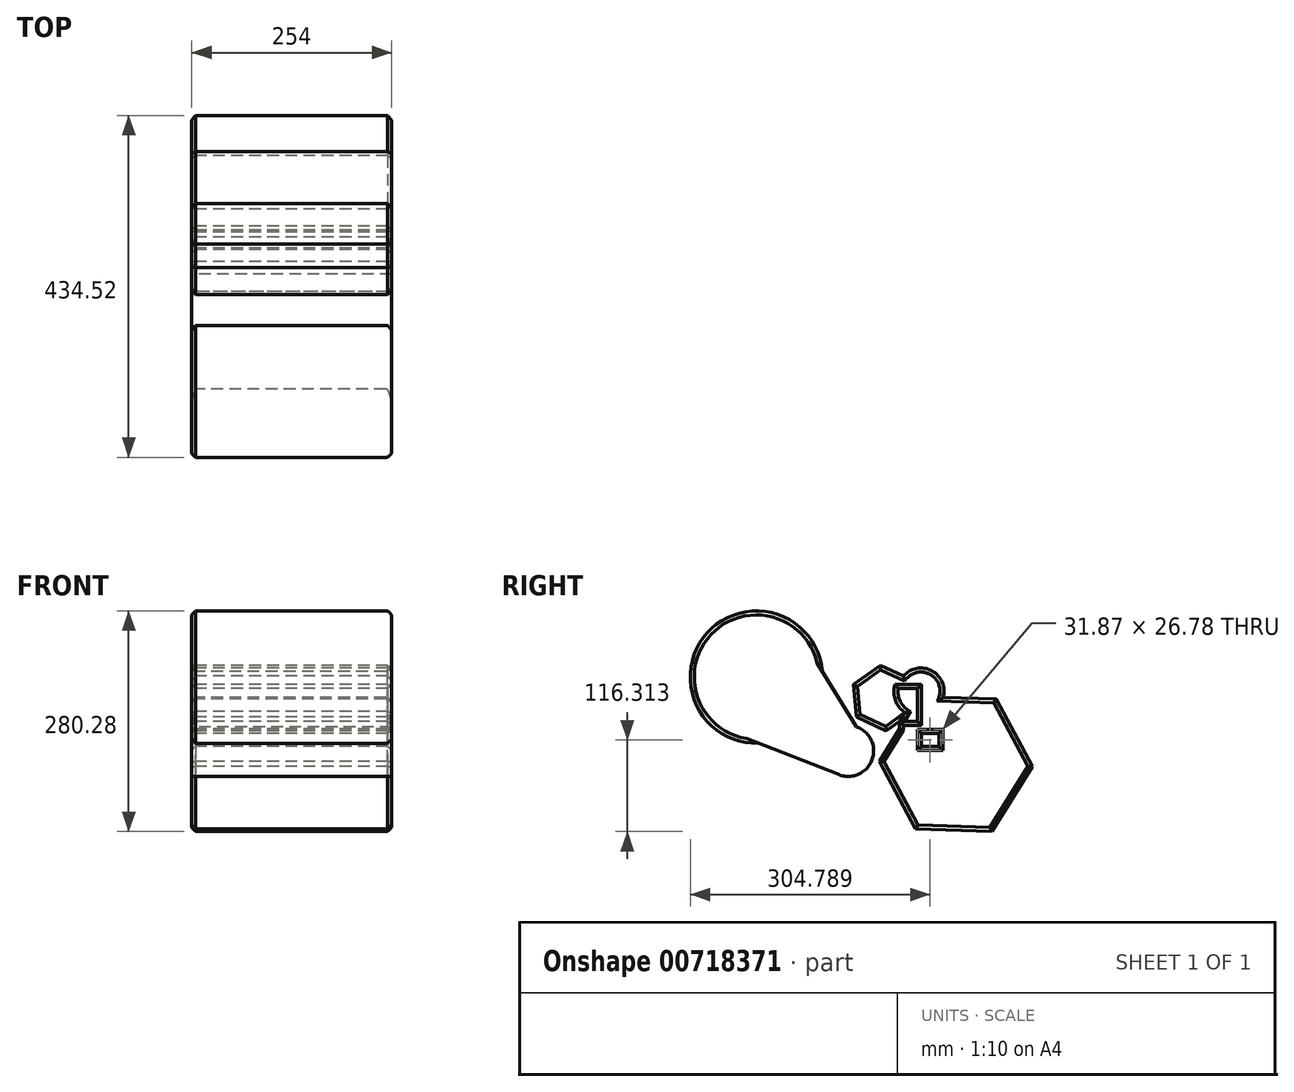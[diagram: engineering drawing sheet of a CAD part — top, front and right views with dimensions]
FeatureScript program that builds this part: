
annotation { "Feature Type Name" : "Feature", "Feature Type Description" : "" }
export const myFeature = defineFeature(function(context is Context, id is Id, definition is map)
    precondition{}
    {
        {
            var Q0;
            Q0=qCreatedBy(makeId("Right.planeOp"),FACE);
            var sketch = newSketch(context, id + "F0", { "sketchPlane" : qUnion([Q0])});
            skCircle(sketch, "E0", {"center": v(-256.47, 191.7) * mm, "radius": 29.3 * mm});
            skLineSegment(sketch, "E1.bottom", {"start": v(-324.32, 195.33) * mm, "end": v(-261, 195.33) * mm});
            skLineSegment(sketch, "E1.top", {"start": v(-324.32, 153.22) * mm, "end": v(-261, 153.22) * mm});
            skLineSegment(sketch, "E1.left", {"start": v(-324.32, 195.33) * mm, "end": v(-324.32, 153.22) * mm});
            skLineSegment(sketch, "E1.right", {"start": v(-261, 195.33) * mm, "end": v(-261, 153.22) * mm});
            skLineSegment(sketch, "E2.bottom", {"start": v(-233.85, 130.77) * mm, "end": v(-283.61, 130.77) * mm});
            skLineSegment(sketch, "E2.top", {"start": v(-233.85, 153.22) * mm, "end": v(-283.61, 153.22) * mm});
            skLineSegment(sketch, "E2.left", {"start": v(-233.85, 130.77) * mm, "end": v(-233.85, 153.22) * mm});
            skLineSegment(sketch, "E2.right", {"start": v(-283.61, 130.77) * mm, "end": v(-283.61, 153.22) * mm});
            skLineSegment(sketch, "E3.bottom", {"start": v(-255.57, 121.25) * mm, "end": v(-233.85, 121.25) * mm});
            skLineSegment(sketch, "E3.top", {"start": v(-255.57, 137.87) * mm, "end": v(-233.85, 137.87) * mm});
            skLineSegment(sketch, "E3.left", {"start": v(-255.57, 121.25) * mm, "end": v(-255.57, 137.87) * mm});
            skLineSegment(sketch, "E3.right", {"start": v(-233.85, 121.25) * mm, "end": v(-233.85, 137.87) * mm});
            skCircle(sketch, "E4.cCircle", {"center": v(-304.42, 182.76) * mm, "radius": 36.14 * mm, "construction": true});
            skLineSegment(sketch, "E4.0", {"start": v(-266.55, 165.23) * mm, "end": v(-300.67, 141.2) * mm});
            skLineSegment(sketch, "E4.1", {"start": v(-300.67, 141.2) * mm, "end": v(-338.54, 158.74) * mm});
            skLineSegment(sketch, "E4.2", {"start": v(-338.54, 158.74) * mm, "end": v(-342.28, 200.3) * mm});
            skLineSegment(sketch, "E4.3", {"start": v(-342.28, 200.3) * mm, "end": v(-308.17, 224.32) * mm});
            skLineSegment(sketch, "E4.4", {"start": v(-308.17, 224.32) * mm, "end": v(-270.3, 206.8) * mm});
            skLineSegment(sketch, "E4.5", {"start": v(-270.3, 206.8) * mm, "end": v(-266.55, 165.23) * mm});
            skPoint(sketch, "E4.0.midPoint", {"position": v(-283.61, 153.22) * mm});
            skCircle(sketch, "E5.cCircle", {"center": v(-212.14, 99.02) * mm, "radius": 84.2 * mm, "construction": true});
            skLineSegment(sketch, "E5.0", {"start": v(-309.3, 102.27) * mm, "end": v(-257.91, 184.8) * mm});
            skLineSegment(sketch, "E5.1", {"start": v(-257.91, 184.8) * mm, "end": v(-160.75, 181.54) * mm});
            skLineSegment(sketch, "E5.2", {"start": v(-160.75, 181.54) * mm, "end": v(-114.98, 95.77) * mm});
            skLineSegment(sketch, "E5.3", {"start": v(-114.98, 95.77) * mm, "end": v(-166.37, 13.25) * mm});
            skLineSegment(sketch, "E5.4", {"start": v(-166.37, 13.25) * mm, "end": v(-263.54, 16.5) * mm});
            skLineSegment(sketch, "E5.5", {"start": v(-263.54, 16.5) * mm, "end": v(-309.3, 102.27) * mm});
            skPoint(sketch, "E5.0.midPoint", {"position": v(-283.61, 143.53) * mm});
            skCircle(sketch, "E6", {"center": v(-465.45, 209.48) * mm, "radius": 84.05 * mm});
            skCircle(sketch, "E7", {"center": v(-348.75, 115.61) * mm, "radius": 32.29 * mm});
            skLineSegment(sketch, "E8", {"start": v(-462.75, 125.48) * mm, "end": v(-360.5, 85.54) * mm});
            skLineSegment(sketch, "E9", {"start": v(-365.03, 86.67) * mm, "end": v(-360.5, 85.54) * mm});
            skLineSegment(sketch, "E10", {"start": v(-338.54, 146.24) * mm, "end": v(-381.69, 216.41) * mm});
            skSolve(sketch);
        }
        {
            var Q0;
            Q0 = qSketchRegion(id + "F0", true);
            extrude(context, id + "F1", {"entities" : qUnion([Q0]), "depth" : 254 * mm, "offsetDistance" : 25.4 * mm});
        }
        {
            var Q0;
            Q0=makeQuery(id+"F1.opExtrude","CAP_EDGE",EDGE,{"disambiguationData":[OSD([sQuery(id+"F0.wireOp",EDGE,"E6")])],"isStart":true});
            var Q1;
            Q1=makeQuery(id+"F1.opExtrude","CAP_EDGE",EDGE,{"disambiguationData":[OSD([sQuery(id+"F0.wireOp",EDGE,"E5.1")])],"isStart":true});
            var Q2;
            Q2=makeQuery(id+"F1.opExtrude","CAP_FACE",FACE,{"disambiguationData":[OSD([sQuery(id+"F0.wireOp",EDGE,"E0"),sQuery(id+"F0.wireOp",EDGE,"E1.bottom"),sQuery(id+"F0.wireOp",EDGE,"E1.right"),sQuery(id+"F0.wireOp",EDGE,"E2.top"),sQuery(id+"F0.wireOp",EDGE,"E2.right"),sQuery(id+"F0.wireOp",EDGE,"E3.bottom"),sQuery(id+"F0.wireOp",EDGE,"E3.top"),sQuery(id+"F0.wireOp",EDGE,"E3.left"),sQuery(id+"F0.wireOp",EDGE,"E3.right"),sQuery(id+"F0.wireOp",EDGE,"E4.0"),sQuery(id+"F0.wireOp",EDGE,"E4.1"),sQuery(id+"F0.wireOp",EDGE,"E4.2"),sQuery(id+"F0.wireOp",EDGE,"E4.3"),sQuery(id+"F0.wireOp",EDGE,"E4.4"),sQuery(id+"F0.wireOp",EDGE,"E5.0"),sQuery(id+"F0.wireOp",EDGE,"E5.1"),sQuery(id+"F0.wireOp",EDGE,"E5.2"),sQuery(id+"F0.wireOp",EDGE,"E5.3"),sQuery(id+"F0.wireOp",EDGE,"E5.4"),sQuery(id+"F0.wireOp",EDGE,"E5.5")])],"isStart":true});
            chamfer(context, id + "F2", {"entities" : qUnion([Q0, Q1, Q2]), "width" : 5.08 * mm, "tangentPropagation" : true});
        }
        {
            var Q0;
            Q0=makeQuery(id+"F1.opExtrude","CAP_EDGE",EDGE,{"disambiguationData":[OSD([sQuery(id+"F0.wireOp",EDGE,"E6")])],"isStart":false});
            var Q1;
            Q1=makeQuery(id+"F1.opExtrude","CAP_EDGE",EDGE,{"disambiguationData":[OSD([sQuery(id+"F0.wireOp",EDGE,"E4.3")])],"isStart":false});
            var Q2;
            Q2=makeQuery(id+"F1.opExtrude","CAP_EDGE",EDGE,{"disambiguationData":[OSD([sQuery(id+"F0.wireOp",EDGE,"E1.bottom")])],"isStart":false});
            var Q3;
            Q3=makeQuery(id+"F1.opExtrude","CAP_EDGE",EDGE,{"disambiguationData":[OSD([sQuery(id+"F0.wireOp",EDGE,"E4.4")])],"isStart":false});
            var Q4;
            Q4=makeQuery(id+"F1.opExtrude","CAP_FACE",FACE,{"disambiguationData":[OSD([sQuery(id+"F0.wireOp",EDGE,"E0"),sQuery(id+"F0.wireOp",EDGE,"E1.bottom"),sQuery(id+"F0.wireOp",EDGE,"E1.right"),sQuery(id+"F0.wireOp",EDGE,"E2.top"),sQuery(id+"F0.wireOp",EDGE,"E2.right"),sQuery(id+"F0.wireOp",EDGE,"E3.bottom"),sQuery(id+"F0.wireOp",EDGE,"E3.top"),sQuery(id+"F0.wireOp",EDGE,"E3.left"),sQuery(id+"F0.wireOp",EDGE,"E3.right"),sQuery(id+"F0.wireOp",EDGE,"E4.0"),sQuery(id+"F0.wireOp",EDGE,"E4.1"),sQuery(id+"F0.wireOp",EDGE,"E4.2"),sQuery(id+"F0.wireOp",EDGE,"E4.3"),sQuery(id+"F0.wireOp",EDGE,"E4.4"),sQuery(id+"F0.wireOp",EDGE,"E5.0"),sQuery(id+"F0.wireOp",EDGE,"E5.1"),sQuery(id+"F0.wireOp",EDGE,"E5.2"),sQuery(id+"F0.wireOp",EDGE,"E5.3"),sQuery(id+"F0.wireOp",EDGE,"E5.4"),sQuery(id+"F0.wireOp",EDGE,"E5.5")])],"isStart":false});
            chamfer(context, id + "F3", {"entities" : qUnion([Q0, Q1, Q2, Q3, Q4]), "width" : 5.08 * mm, "tangentPropagation" : true});
        }
        {
            var Q0;
            {var subQ0=sQuery(id+"F0.wireOp",EDGE,"E5.1");Q0=makeQuery(id+"F3.opChamfer","BLEND_EDGE",EDGE,{"blendedFrom":[makeQuery(id+"F1.opExtrude","CAP_EDGE",EDGE,{"disambiguationData":[OSD([subQ0])],"isStart":false}),makeQuery(id+"F1.opExtrude","SWEPT_FACE",FACE,{"disambiguationData":[OSD([subQ0])]})],"blendedInto":[makeQuery(id+"F1.opExtrude","SWEPT_FACE",FACE,{"disambiguationData":[OSD([subQ0])]})]});}
            fillet(context, id + "F4", {"entities" : qUnion([Q0]), "radius" : 5.08 * mm, "tangentPropagation" : true, "allowEdgeOverflow" : false});
        }
        {
            var Q0;
            {var subQ0=sQuery(id+"F0.wireOp",EDGE,"E6");Q0=makeQuery(id+"F3.opChamfer","BLEND_EDGE",EDGE,{"blendedFrom":[makeQuery(id+"F1.opExtrude","CAP_EDGE",EDGE,{"disambiguationData":[OSD([subQ0])],"isStart":false}),makeQuery(id+"F1.opExtrude","SWEPT_FACE",FACE,{"disambiguationData":[OSD([subQ0])]})],"blendedInto":[makeQuery(id+"F1.opExtrude","SWEPT_FACE",FACE,{"disambiguationData":[OSD([subQ0])]})]});}
            fillet(context, id + "F5", {"entities" : qUnion([Q0]), "radius" : 5.08 * mm, "tangentPropagation" : true, "allowEdgeOverflow" : false});
        }
    });
